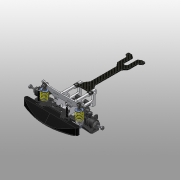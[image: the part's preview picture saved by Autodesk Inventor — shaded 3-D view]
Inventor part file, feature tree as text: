
AUTODESK INVENTOR PART (.ipt)
format: ipt  version: 2016 (Build 200138000, 138)  size: 8,970,752 bytes
history: native  units: mm
features: other x88, sketch x4
ambient origin geometry x8: Origin, YZ Plane, XZ Plane, XY Plane, X Axis, Y Axis, Z Axis, Center Point
bodies: Solid1 (feature_tree)
feature tree (92):
  other  "100-003.iam"
  other  "300-004.iam:1::500-133.ipt:1"
  other  "300-004.iam:1::500-132.ipt:1"
  other  "300-004.iam:1::500-131.ipt:1"
  other  "500-010.ipt:1"
  other  "500-009.ipt:2"
  other  "M3-6.ipt:14"
  other  "M3-6.ipt:15"
  other  "500-171.ipt:1"
  other  "500-172.ipt:1"
  other  "500-169.ipt:1"
  other  "500-172.ipt:2"
  other  "500-171.ipt:2"
  other  "500-169.ipt:2"
  other  "500-124.ipt:1"
  other  "BS 4168 : Part 6  Hexagon Socket Button Head Screw  - Metric M3 x 8:3"
  other  "BS 4168 : Part 6  Hexagon Socket Button Head Screw  - Metric M3 x 8:4"
  other  "M3.ipt:1"
  other  "M3-10.ipt:1"
  other  "M3.ipt:2"
  other  "M3-10.ipt:2"
  other  "500-170.ipt:1"
  other  "300-025.iam:1::300-028.iam:1::21 D - 10 x 14 x 7.ipt:1"
  other  "300-025.iam:1::300-028.iam:1::21 D - 10 x 14 x 7.ipt:2"
  other  "300-025.iam:1::300-028.iam:1::500-140.ipt:1"
  other  "300-025.iam:1::500-126.ipt:2"
  other  "300-025.iam:1::M4.ipt:1"
  other  "300-007.iam:1::500-173.ipt:1"
  other  "300-007.iam:1::500-109.ipt:1"
  other  "300-007.iam:1::BS 4168 : Part 6  Hexagon Socket Button Head Screw  - Metric M3 x 8:1"
  other  "300-007.iam:1::BS 4168 : Part 6  Hexagon Socket Button Head Screw  - Metric M3 x 8:2"
  other  "300-009-04.iam:1::500-000.ipt:1"
  other  "300-009-04.iam:1::500-000.ipt:2"
  other  "300-009-04.iam:1::500-001-02.ipt:1"
  other  "500-109.ipt:1"
  other  "300-010.iam:1::500-106.ipt:1"
  other  "300-010.iam:1::500-100.ipt:1"
  other  "300-010.iam:1::500-102.ipt:1"
  other  "300-010.iam:1::500-104.ipt:1"
  other  "300-010.iam:1::500-109.ipt:1"
  other  "300-010.iam:1::500-109.ipt:2"
  other  "300-010.iam:1::500-107.ipt:1"
  other  "300-010.iam:1::500-105.ipt:1"
  other  "300-010.iam:1::500-103.ipt:2"
  other  "300-010.iam:1::Compression Spring 16:1"
  other  "500-175.ipt:1"
  other  "300-027.iam:1::300-020.iam:1::21 D - 10 x 14 x 7.ipt:1"
  other  "300-027.iam:1::300-020.iam:1::21 D - 10 x 14 x 7.ipt:2"
  other  "300-027.iam:1::300-020.iam:1::500-134.ipt:1"
  other  "300-027.iam:1::500-129.ipt:2"
  other  "300-027.iam:1::M4.ipt:1"
  other  "300-007.iam:2::500-173.ipt:1"
  other  "300-007.iam:2::500-109.ipt:1"
  other  "300-007.iam:2::BS 4168 : Part 6  Hexagon Socket Button Head Screw  - Metric M3 x 8:1"
  other  "300-007.iam:2::BS 4168 : Part 6  Hexagon Socket Button Head Screw  - Metric M3 x 8:2"
  other  "300-010.iam:2::500-106.ipt:1"
  other  "300-010.iam:2::500-100.ipt:1"
  other  "300-010.iam:2::500-102.ipt:1"
  other  "300-010.iam:2::500-104.ipt:1"
  other  "300-010.iam:2::500-109.ipt:1"
  other  "300-010.iam:2::500-109.ipt:2"
  other  "300-010.iam:2::500-107.ipt:1"
  other  "300-010.iam:2::500-105.ipt:1"
  other  "300-010.iam:2::500-103.ipt:2"
  other  "300-010.iam:2::Compression Spring 16:1"
  other  "300-009-04.iam:2::500-000.ipt:1"
  other  "300-009-04.iam:2::500-000.ipt:2"
  other  "300-009-04.iam:2::500-001-02.ipt:1"
  other  "500-109.ipt:2"
  other  "500-010.ipt:2"
  other  "300-032.iam:1::500-180.ipt:1"
  other  "300-032.iam:1::500-179.ipt:1"
  other  "300-032.iam:1::500-177.ipt:1"
  other  "300-032.iam:2::500-180.ipt:1"
  other  "300-032.iam:2::500-179.ipt:1"
  other  "300-032.iam:2::500-177.ipt:1"
  other  "BS 4168 : Part 6  Hexagon Socket Button Head Screw  - Metric M3 x 8:5"
  other  "BS 4168 : Part 6  Hexagon Socket Button Head Screw  - Metric M3 x 8:6"
  other  "M3-10.ipt:3"
  other  "M3-10.ipt:4"
  other  "Work Point1"
  other  "Work Point1_1"
  other  "Work Point1_2"
  sketch  "Sketch9"
  sketch  "Sketch9_1"  dims[d0=10.0mm]
  other  "Work Point1_3"
  other  "Work Point1_4"
  sketch  "Sketch9_2"  dims[d31=0.5mm]
  sketch  "Sketch9_3"
  other  "Work Point1_5"
  other  "Work Point1_6"
  other  "Work Point1_7"
